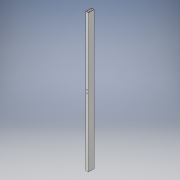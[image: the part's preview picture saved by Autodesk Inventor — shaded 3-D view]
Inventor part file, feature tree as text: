
AUTODESK INVENTOR PART (.ipt)
format: ipt  version: 2017 (Build 210142000, 142)  size: 123,904 bytes
history: native  units: in
note: dims shown in document units (in); Inventor stores cm internally (conversion verified against a paired STEP export)
features: extrude x3, sketch x3
ambient origin geometry x8: Origin, YZ Plane, XZ Plane, XY Plane, X Axis, Y Axis, Z Axis, Center Point
bodies: Solid1 (feature_tree)
feature tree (6):
  extrude  "Extrusion1"  Depth=2.0in
  extrude  "Extrusion2"  Depth=1.75in
  extrude  "Extrusion3"  Depth=0.125in
  sketch  "Sketch2"  dims[d2=1.0in d3=2.0in]
  sketch  "Sketch3"  dims[d4=0.75in d5=1.75in]
  sketch  "Sketch4"  dims[d6=0.125in d7=0.125in d8=48.0in d9=0.0in d10=48.0in d11=24.0in d12=0.5in d13=0.25in d14=48.0in d15=0.0in d16=1.125in d17=1.125in d18=0.25in d19=0.0in]
